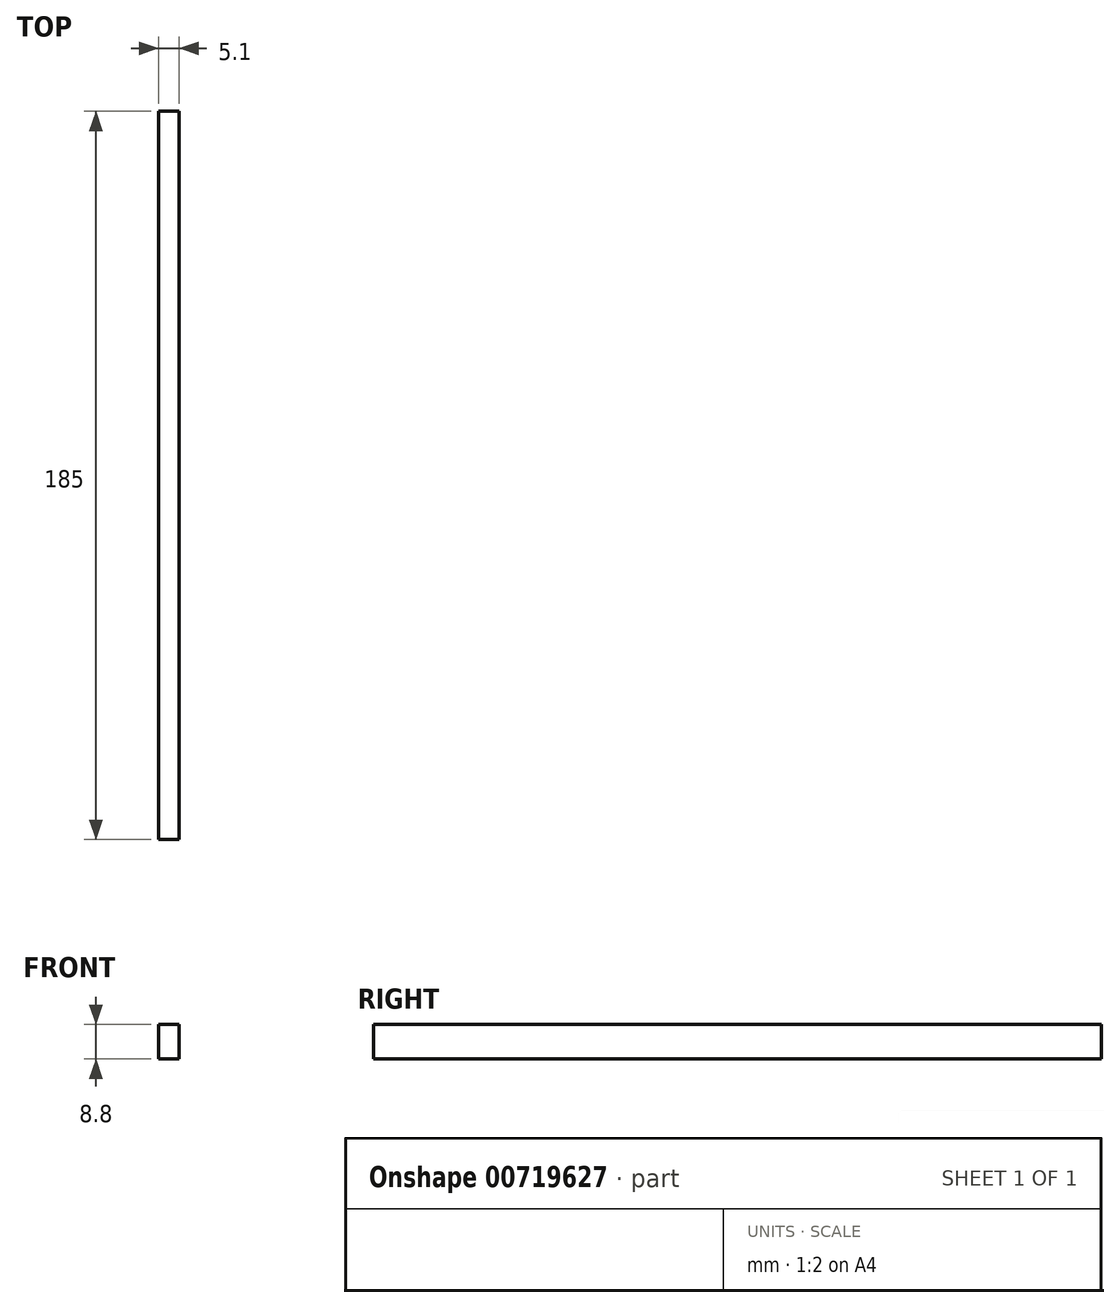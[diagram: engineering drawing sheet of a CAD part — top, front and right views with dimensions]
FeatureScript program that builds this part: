
annotation { "Feature Type Name" : "Feature", "Feature Type Description" : "" }
export const myFeature = defineFeature(function(context is Context, id is Id, definition is map)
    precondition{}
    {
        {
            var Q0;
            Q0=qCreatedBy(makeId("Front.planeOp"),FACE);
            var sketch = newSketch(context, id + "F0", { "sketchPlane" : qUnion([Q0])});
            skLineSegment(sketch, "E0.bottom", {"start": v(-17.35, 14.38) * mm, "end": v(-12.25, 14.38) * mm});
            skLineSegment(sketch, "E0.top", {"start": v(-17.35, 5.58) * mm, "end": v(-12.25, 5.58) * mm});
            skLineSegment(sketch, "E0.left", {"start": v(-17.35, 14.38) * mm, "end": v(-17.35, 5.58) * mm});
            skLineSegment(sketch, "E0.right", {"start": v(-12.25, 14.38) * mm, "end": v(-12.25, 5.58) * mm});
            skSolve(sketch);
        }
        {
            var Q0;
            Q0=makeQuery(id+"F0.imprint","IMPRINT",FACE,{"disambiguationData":[TD([[makeQuery(id+"F0.imprint","IMPRINT",EDGE,{"derivedFrom":sQuery(id+"F0.wireOp",EDGE,"E0.bottom")}),-1.0]])]});
            extrude(context, id + "F1", {"entities" : qUnion([Q0]), "depth" : 185 * mm});
        }
    });
